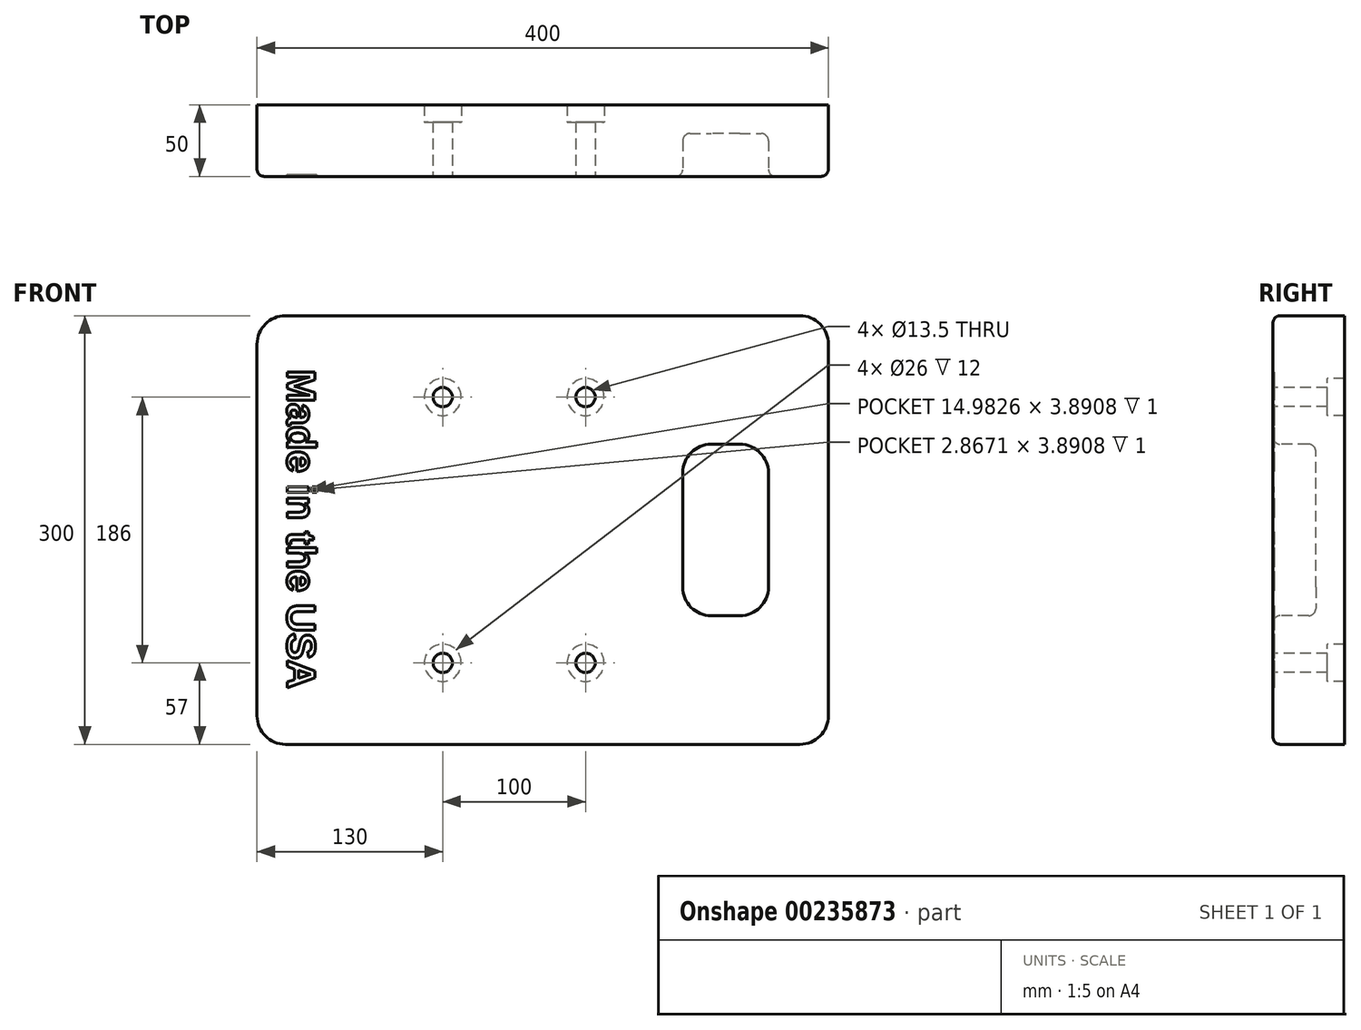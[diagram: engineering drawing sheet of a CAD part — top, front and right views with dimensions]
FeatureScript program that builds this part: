
annotation { "Feature Type Name" : "Feature", "Feature Type Description" : "" }
export const myFeature = defineFeature(function(context is Context, id is Id, definition is map)
    precondition{}
    {
        {
            var Q0;
            Q0=qCreatedBy(makeId("Front.planeOp"),FACE);
            var sketch = newSketch(context, id + "F0", { "sketchPlane" : qUnion([Q0])});
            skLineSegment(sketch, "E0", {"start": v(0, 20) * mm, "end": v(0, 280) * mm});
            skLineSegment(sketch, "E1", {"start": v(-20, 300) * mm, "end": v(-380, 300) * mm});
            skLineSegment(sketch, "E2", {"start": v(-400, 280) * mm, "end": v(-400, 20) * mm});
            skLineSegment(sketch, "E3", {"start": v(-380, 0) * mm, "end": v(-20, 0) * mm});
            skPoint(sketch, "E4.visualSharp", {"position": v(-400, 300) * mm});
            skArc(sketch, "E4.filletArc", {"start": v(-380, 300) * mm, "mid": v(-394.14, 294.14) * mm, "end": v(-400, 280) * mm});
            skPoint(sketch, "E5.visualSharp", {"position": v(-400, 0) * mm});
            skArc(sketch, "E5.filletArc", {"start": v(-400, 20) * mm, "mid": v(-394.14, 5.86) * mm, "end": v(-380, 0) * mm});
            skPoint(sketch, "E6.visualSharp", {"position": v(0, 0) * mm});
            skArc(sketch, "E6.filletArc", {"start": v(-20, 0) * mm, "mid": v(-5.86, 5.86) * mm, "end": v(0, 20) * mm});
            skPoint(sketch, "E7.visualSharp", {"position": v(0, 300) * mm});
            skArc(sketch, "E7.filletArc", {"start": v(0, 280) * mm, "mid": v(-5.86, 294.14) * mm, "end": v(-20, 300) * mm});
            skLineSegment(sketch, "E8", {"start": v(-400, 0) * mm, "end": v(-102, 0) * mm, "construction": true});
            skLineSegment(sketch, "E9", {"start": v(-102, 0) * mm, "end": v(-42, 0) * mm, "construction": true});
            skLineSegment(sketch, "E10", {"start": v(0, 0) * mm, "end": v(0, 150) * mm, "construction": true});
            skLineSegment(sketch, "E11", {"start": v(0, 210) * mm, "end": v(0, 90) * mm});
            skLineSegment(sketch, "E12", {"start": v(-102, 110) * mm, "end": v(-102, 190) * mm});
            skLineSegment(sketch, "E13", {"start": v(-42, 110) * mm, "end": v(-42, 190) * mm});
            skLineSegment(sketch, "E14", {"start": v(-62, 210) * mm, "end": v(-82, 210) * mm});
            skLineSegment(sketch, "E15", {"start": v(-62, 90) * mm, "end": v(-82, 90) * mm});
            skPoint(sketch, "E16.visualSharp", {"position": v(-102, 210) * mm});
            skArc(sketch, "E16.filletArc", {"start": v(-82, 210) * mm, "mid": v(-96.14, 204.14) * mm, "end": v(-102, 190) * mm});
            skPoint(sketch, "E17.visualSharp", {"position": v(-102, 90) * mm});
            skArc(sketch, "E17.filletArc", {"start": v(-102, 110) * mm, "mid": v(-96.14, 95.86) * mm, "end": v(-82, 90) * mm});
            skPoint(sketch, "E18.visualSharp", {"position": v(-42, 90) * mm});
            skArc(sketch, "E18.filletArc", {"start": v(-62, 90) * mm, "mid": v(-47.86, 95.86) * mm, "end": v(-42, 110) * mm});
            skPoint(sketch, "E19.visualSharp", {"position": v(-42, 210) * mm});
            skArc(sketch, "E19.filletArc", {"start": v(-42, 190) * mm, "mid": v(-47.86, 204.14) * mm, "end": v(-62, 210) * mm});
            skLineSegment(sketch, "E20", {"start": v(-380, 280) * mm, "end": v(-280, 280) * mm, "construction": true});
            skLineSegment(sketch, "E21", {"start": v(-380, 280) * mm, "end": v(-380, 20) * mm, "construction": true});
            skSolve(sketch);
        }
        {
            var Q0;
            Q0=makeQuery(id+"F0.imprint","IMPRINT",FACE,{"disambiguationData":[TD([[makeQuery(id+"F0.imprint","IMPRINT",EDGE,{"derivedFrom":sQuery(id+"F0.wireOp",EDGE,"E12")}),-1.0]])]});
            var Q1;
            Q1=makeQuery(id+"F0.imprint","IMPRINT",FACE,{"disambiguationData":[TD([[makeQuery(id+"F0.imprint","IMPRINT",EDGE,{"derivedFrom":sQuery(id+"F0.wireOp",EDGE,"E1")}),1.0]])]});
            extrude(context, id + "F1", {"entities" : qUnion([Q0, Q1]), "oppositeDirection" : true, "depth" : 50 * mm});
        }
        {
            var Q0;
            Q0=makeQuery(id+"F0.imprint","IMPRINT",FACE,{"disambiguationData":[TD([[makeQuery(id+"F0.imprint","IMPRINT",EDGE,{"derivedFrom":sQuery(id+"F0.wireOp",EDGE,"E12")}),-1.0]])]});
            extrude(context, id + "F2", {"entities" : qUnion([Q0]), "operationType" : NewBodyOperationType.REMOVE, "oppositeDirection" : true, "depth" : 30 * mm});
        }
        {
            var Q0;
            Q0=makeQuery(id+"F1.opExtrude","CAP_FACE",FACE,{"disambiguationData":[OSD([sQuery(id+"F0.wireOp",EDGE,"E0"),sQuery(id+"F0.wireOp",EDGE,"E1"),sQuery(id+"F0.wireOp",EDGE,"E2"),sQuery(id+"F0.wireOp",EDGE,"E3"),sQuery(id+"F0.wireOp",EDGE,"E4.filletArc"),sQuery(id+"F0.wireOp",EDGE,"E5.filletArc"),sQuery(id+"F0.wireOp",EDGE,"E6.filletArc"),sQuery(id+"F0.wireOp",EDGE,"E7.filletArc"),sQuery(id+"F0.wireOp",EDGE,"E11")])],"isStart":true});
            var Q1;
            Q1=makeQuery(id+"F2.boolean.opBoolean","COPY",FACE,{"derivedFrom":makeQuery(id+"F2.opExtrude","CAP_FACE",FACE,{"disambiguationData":[OSD([sQuery(id+"F0.wireOp",EDGE,"E12"),sQuery(id+"F0.wireOp",EDGE,"E13"),sQuery(id+"F0.wireOp",EDGE,"E14"),sQuery(id+"F0.wireOp",EDGE,"E15"),sQuery(id+"F0.wireOp",EDGE,"E16.filletArc"),sQuery(id+"F0.wireOp",EDGE,"E17.filletArc"),sQuery(id+"F0.wireOp",EDGE,"E18.filletArc"),sQuery(id+"F0.wireOp",EDGE,"E19.filletArc")])],"isStart":false})});
            fillet(context, id + "F3", {"entities" : qUnion([Q0, Q1]), "radius" : 5 * mm, "tangentPropagation" : true, "allowEdgeOverflow" : false});
        }
        {
            var Q0;
            Q0=qCreatedBy(makeId("Front.planeOp"),FACE);
            cPlane(context, id + "F4", {"entities" : qUnion([Q0]), "cplaneType" : CPlaneType.OFFSET, "offset" : 50 * mm, "oppositeDirection" : true, "width" : 150 * mm, "height" : 150 * mm});
        }
        {
            var Q0;
            Q0=qCreatedBy(id+"F4.planeOp",FACE);
            var sketch = newSketch(context, id + "F5", { "sketchPlane" : qUnion([Q0])});
            skLineSegment(sketch, "E22", {"start": v(0, 0) * mm, "end": v(-170, 0) * mm, "construction": true});
            skLineSegment(sketch, "E23", {"start": v(-170, 0) * mm, "end": v(-270, 0) * mm, "construction": true});
            skLineSegment(sketch, "E24", {"start": v(-270, 0) * mm, "end": v(-270, 150) * mm, "construction": true});
            skLineSegment(sketch, "E25", {"start": v(-270, 150) * mm, "end": v(-270, 243) * mm, "construction": true});
            skLineSegment(sketch, "E26", {"start": v(-270, 243) * mm, "end": v(-270, 57) * mm, "construction": true});
            skLineSegment(sketch, "E27", {"start": v(-170, 0) * mm, "end": v(-170, 243) * mm, "construction": true});
            skLineSegment(sketch, "E28", {"start": v(-270, 57) * mm, "end": v(-170, 57) * mm, "construction": true});
            skSolve(sketch);
        }
        {
            var Q0;
            Q0=sQuery(id+"F5.wireOp",VERTEX,"E27.end");
            var Q1;
            Q1=sQuery(id+"F5.wireOp",VERTEX,"E26.start");
            var Q2;
            Q2=sQuery(id+"F5.wireOp",VERTEX,"E28.start");
            var Q3;
            Q3=sQuery(id+"F5.wireOp",VERTEX,"E28.end");
            var Q4;
            Q4=makeQuery(id+"F1.opExtrude","SWEPT_BODY",BODY,{"disambiguationData":[OSD([sQuery(id+"F0.wireOp",EDGE,"E0"),sQuery(id+"F0.wireOp",EDGE,"E1"),sQuery(id+"F0.wireOp",EDGE,"E2"),sQuery(id+"F0.wireOp",EDGE,"E3"),sQuery(id+"F0.wireOp",EDGE,"E4.filletArc"),sQuery(id+"F0.wireOp",EDGE,"E5.filletArc"),sQuery(id+"F0.wireOp",EDGE,"E6.filletArc"),sQuery(id+"F0.wireOp",EDGE,"E7.filletArc"),sQuery(id+"F0.wireOp",EDGE,"E11")])]});
            hole(context, id + "F6", {"style" : HoleStyle.C_BORE, "endStyle" : HoleEndStyle.THROUGH, "oppositeDirection" : true, "holeDiameter" : 13.5 * mm, "cBoreDiameter" : 26 * mm, "cBoreDepth" : 12 * mm, "isTappedThrough" : true, "tappedDepth" : 3.5 * mm, "tapClearance" : 3, "startFromSketch" : true, "locations" : qUnion([Q0, Q1, Q2, Q3]), "scope" : qUnion([Q4])});
        }
        {
            var Q0;
            Q0=qCreatedBy(makeId("Front.planeOp"),FACE);
            var sketch = newSketch(context, id + "F7", { "sketchPlane" : qUnion([Q0])});
            skText(sketch, "E29", { "text": "Made in the USA", "fontName": "Arimo-Bold.ttf"});
            skLineSegment(sketch, "E30", {"start": v(-358.46, 293.16) * mm, "end": v(-358.46, 262.48) * mm, "construction": true});
            const initialGuessF7  = {"E29": [-0.37888, 0.26248, 0, -1, 0.02042]};
            skSetInitialGuess(sketch, initialGuessF7);
            skSolve(sketch);
        }
        {
            var Q0;
            Q0 = qSketchRegion(id + "F7", true);
            extrude(context, id + "F8", {"entities" : qUnion([Q0]), "operationType" : NewBodyOperationType.REMOVE, "oppositeDirection" : true, "depth" : 1 * mm});
        }
    });
